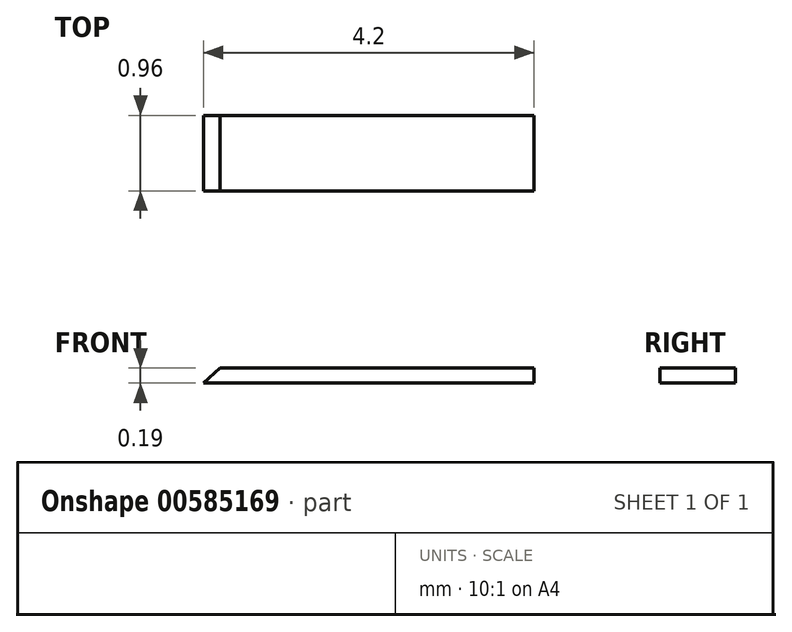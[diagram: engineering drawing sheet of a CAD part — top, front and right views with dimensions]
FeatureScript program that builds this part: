
annotation { "Feature Type Name" : "Feature", "Feature Type Description" : "" }
export const myFeature = defineFeature(function(context is Context, id is Id, definition is map)
    precondition{}
    {
        {
            var Q0;
            Q0=qCreatedBy(makeId("Front.planeOp"),FACE);
            var sketch = newSketch(context, id + "F0", { "sketchPlane" : qUnion([Q0])});
            skLineSegment(sketch, "E0.bottom", {"start": v(0, 0) * mm, "end": v(4.2, 0) * mm});
            skLineSegment(sketch, "E0.top", {"start": v(0.21, 0.19) * mm, "end": v(4.2, 0.19) * mm});
            skLineSegment(sketch, "E0.right", {"start": v(4.2, 0) * mm, "end": v(4.2, 0.19) * mm});
            skLineSegment(sketch, "E1", {"start": v(0, 0) * mm, "end": v(0.21, 0.19) * mm});
            skSolve(sketch);
        }
        {
            var Q0;
            Q0 = qSketchRegion(id + "F0", true);
            extrude(context, id + "F1", {"entities" : qUnion([Q0]), "depth" : 0.96 * mm, "offsetDistance" : 25 * mm});
        }
    });
